# Revit family: РКВ_І 630_1100
name_source: partatom
category: Арматура воздуховодов
units: mm (PartAtom-declared; Revit-internal decimal feet)

## family parameters
Всегда вертикально = Да
На основе рабочей плоскости = Нет
Общий = Нет
При загрузке вырезать с полостями = Нет
Размер круглого соединителя = Использовать диаметр
Тип детали = Присоединяется

## types (12) — shared parameters
00_20_Manufacturer = Вентс
00_20_Name = Монтажна рама
Casing Material = Металл, окрашенный, синий, матовый RAL 5007
Load Classification = HVAC
Maintenance zone material = <По категории>
URL = https://vents.ua
Изготовитель = Вентс
zero-valued in all types: Отметка по умолчанию

## per-type parameters (varying)
| type | B | B1 | B2 | H | L | L1 | L2 | Ln | Вес | Описание | Фаска |
| РКВ 630 | 1212 мм | 852 мм | 413 мм | 600 мм | 912 мм | 750 мм | 459 мм | 917 мм | 65.9 кг |  | 229 мм |
| РКВ 710 | 1262 мм | 902 мм | 438 мм | 600 мм | 962 мм | 840 мм | 484 мм | 967 мм | 68.5 кг |  | 242 мм |
| РКВ 900 | 1512 мм | 1152 мм | 563 мм | 650 мм | 1212 мм | 1050 мм | 609 мм | 1217 мм | 85.7 кг |  | 304 мм |
| РКВ 1000 | 1712 мм | 1352 мм | 663 мм | 730 мм | 1412 мм | 1240 мм | 709 мм | 1417 мм | 103.7 кг |  | 354 мм |
| РКВ 1100 | 1712 мм | 1352 мм | 663 мм | 730 мм | 1412 мм | 1240 мм | 709 мм | 1417 мм | 103.7 кг |  | 354 мм |
| РКВ 800 | 1262 мм | 902 мм | 438 мм | 600 мм | 962 мм | 840 мм | 484 мм | 967 мм | 68.5 кг |  | 242 мм |
| РКВІ 1000 | 1712 мм | 1350 мм | 663 мм | 730 мм | 1412 мм | 1240 мм | 709 мм | 1417 мм | 140.6 кг | Ізольована | 354 мм |
| РКВІ 1100 | 1712 мм | 1350 мм | 663 мм | 730 мм | 1412 мм | 1240 мм | 709 мм | 1417 мм | 140.6 кг | Ізольована | 354 мм |
| РКВІ 630 | 1212 мм | 850 мм | 413 мм | 600 мм | 912 мм | 750 мм | 459 мм | 917 мм | 85.5 кг | Ізольована | 229 мм |
| РКВІ 710 | 1262 мм | 900 мм | 438 мм | 600 мм | 962 мм | 840 мм | 484 мм | 967 мм | 89 кг | Ізольована | 242 мм |
| РКВІ 800 | 1262 мм | 900 мм | 438 мм | 600 мм | 962 мм | 840 мм | 484 мм | 967 мм | 89 кг | Ізольована | 242 мм |
| РКВІ 900 | 1512 мм | 1150 мм | 563 мм | 650 мм | 1212 мм | 1050 мм | 609 мм | 1217 мм | 113 кг | Ізольована | 304 мм |

note: column(s) folded — value = type name in every type: 00_20_Type
